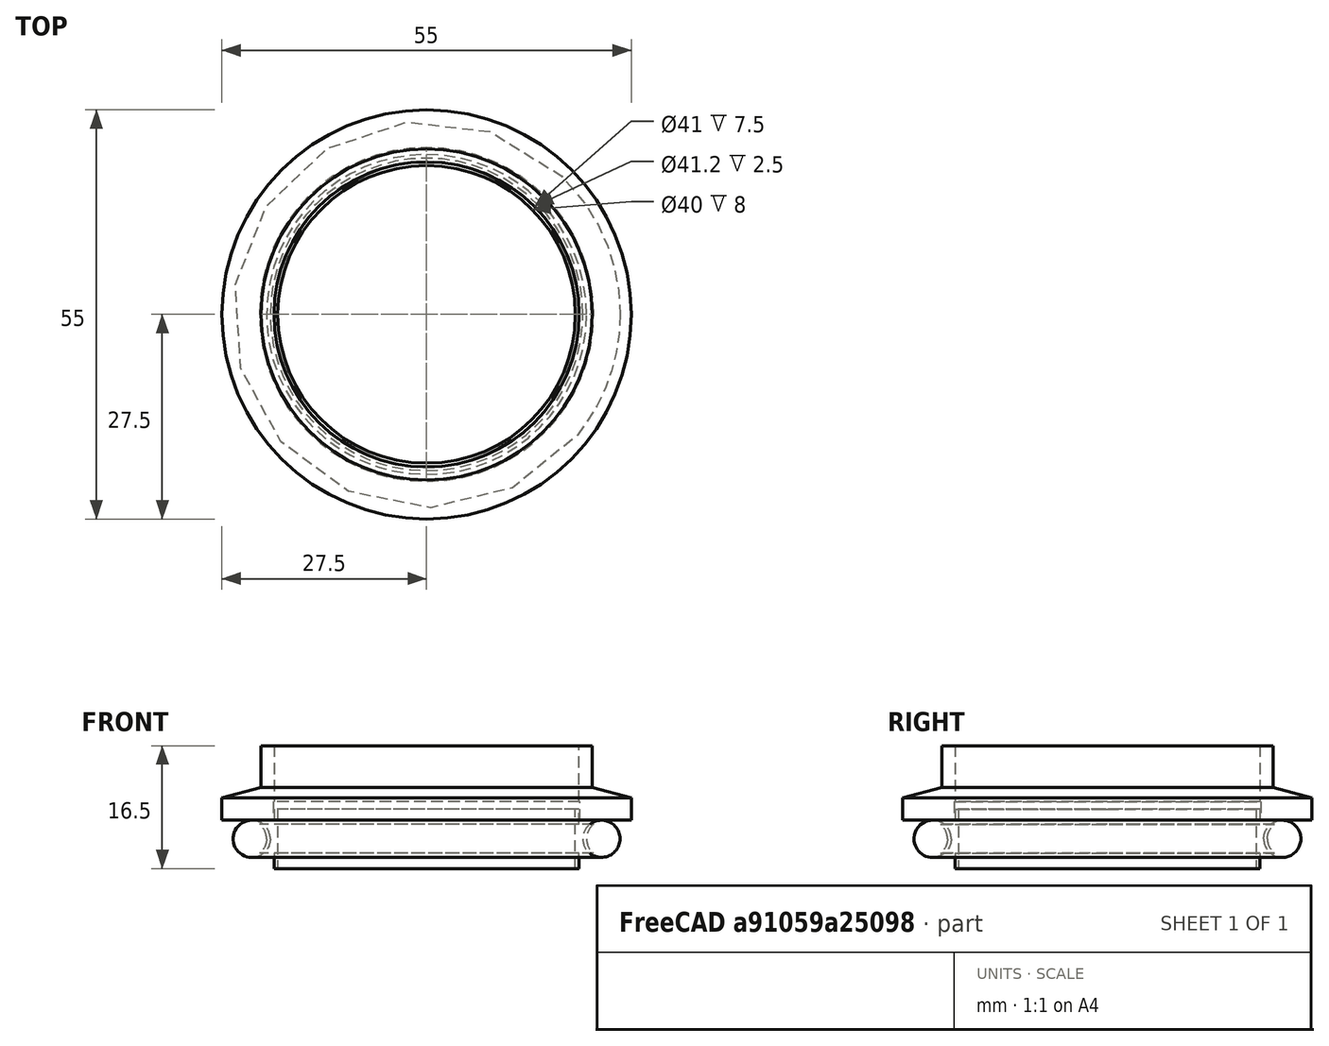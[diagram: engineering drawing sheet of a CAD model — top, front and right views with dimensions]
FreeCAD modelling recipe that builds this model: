
FCSTD DOCUMENT  (FreeCAD 1.0R1.0.0)
Label: KFFlange
License: All rights reserved
LicenseURL: http://en.wikipedia.org/wiki/All_rights_reserved
objects: Part::Cylinder×7, Part::MultiFuse×3, Part::Cut×3, Part::Torus×2, Spreadsheet::Sheet×1, Part::Cone×1
note: 16 computed .brp shape members not serialized (recipe doc carries the construction recipe); baked Part::Feature solids carry a one-line shape summary decoded from their .brp

FEATURE [Spreadsheet::Sheet] Spreadsheet  label="KleinFlange"
  KF = 3
  cells = A1='Nominal bore; B1='D: O-ring ID; C1='d1: Pipe OD; D1='d2: Carrier retainer diameter; E1='d3: Coupling OD; F1='d4: Carrier ID; G1='d5: Connecting Pipe Carrier OD; H1='d6: OD to hold Oring in carrier; I1='R: O ring retainer radius (carrier); A2==hiddenref(.KF.String); B2(D)==.B6; C2(d1)==.C6; D2(d2)==.D6; E2(d3)==.E6; F2(d4)==.F6; G2(d5)==.G6; H2(d6)==.H6; I2(R)=; A3='10; B3=15; C3=14; D3=12.2; E3=30; F3=10; G3=12; H3=15.3; A4='16; B4=18; C4=20; D4=17.2; E4=30; F4=16; G4=17; H4=18.5; A5='25; B5=28; C5=28; D5=26.2; E5=40; F5=25; G5=26; H5=28.5; A6='40; B6=42; C6=44.5; D6=41.2; E6=55; F6=40; G6=41; H6=43; A7='50; B7=55; C7=61; D7=52.2; E7=75; F7=50; G7=52; H7=55.5; A9='O Ring; A10='O ring diameter; B10(oring_dia)=5; A11='Inner diameter; B11==B2; A13='Coupling; L13='Coupling calculated properties; A14='Total length; B14(coupling_len)=10; C14='10 is minimum length; L14='Taper height; M14(coupling_taper_height)==(d3 - d1) / (2 * tan(90 - 15)); A15='Pipe diameter; B15(pipe_dia_user)=100; C15='Maximum specified by d5 (Connecting pipe diameter); L15='Effective pipe diameter; M15(coupling_pipe_ID)==min(d5; pipe_dia_user); L16='Effective coupling length; M16(coupling_len_eff)==min(coupling_len; 10); A17='O Ring carrier interface; A18='O ring carrier recess; B18(oring_recess)=2.5; C18='>= 2.5 by norm
  expr: .KF.Enum = cells[<<A3:|>>]
  expr: .cells.Bind.B2.I2 = tuple(.cells; <<B>> + str(hiddenref(KF) + 3); <<I>> + str(hiddenref(KF) + 3))
FEATURE [Part::Cylinder] Cylinder
  Angle = 360
  AttacherType = Attacher::AttachEngine3D
  FirstAngle = 0
  Height = 3
  Radius = 27.5
  SecondAngle = 0
  expr: Radius = <<KleinFlange>>.d3 / 2
FEATURE [Part::Cone] Cone
  Angle = 360
  AttacherType = Attacher::AttachEngine3D
  Height = 1.40673
  Placement = pos=(0,0,3) rot=(0,0,1;0rad)
  Radius1 = 27.5
  Radius2 = 22.25
  expr: Height = <<KleinFlange>>.coupling_taper_height
  expr: Radius1 = <<KleinFlange>>.d3 / 2
  expr: Radius2 = <<KleinFlange>>.d1 / 2
FEATURE [Part::Cylinder] Cylinder001
  Angle = 360
  AttacherType = Attacher::AttachEngine3D
  FirstAngle = 0
  Height = 10
  Radius = 22.25
  SecondAngle = 0
  expr: Height = <<KleinFlange>>.coupling_len_eff
  expr: Radius = <<KleinFlange>>.d1 / 2
FEATURE [Part::MultiFuse] Fusion
  Shapes = -> [Cylinder001,Cylinder,Cone]
FEATURE [Part::Cylinder] Cylinder002
  Angle = 360
  AttacherType = Attacher::AttachEngine3D
  FirstAngle = 0
  Height = 2.5
  Radius = 20.6
  SecondAngle = 0
  expr: Height = <<KleinFlange>>.oring_recess
  expr: Radius = <<KleinFlange>>.d2 / 2
FEATURE [Part::Cylinder] Cylinder003
  Angle = 360
  AttacherType = Attacher::AttachEngine3D
  FirstAngle = 0
  Height = 10
  Radius = 20.5
  SecondAngle = 0
  expr: Height = <<KleinFlange>>.coupling_len
  expr: Radius = <<KleinFlange>>.coupling_pipe_ID / 2
FEATURE [Part::MultiFuse] Fusion001
  Shapes = -> [Cylinder002,Cylinder003]
FEATURE [Part::Cut] Cut  label="Coupler"
  Base = -> Fusion
  Tool = -> Fusion001
FEATURE [Part::Torus] Torus  label="ORing"
  Angle1 = -180
  Angle2 = 180
  Angle3 = 360
  AttacherType = Attacher::AttachEngine3D
  Placement = pos=(0,0,-2.5) rot=(0,0,1;0rad)
  Radius1 = 23.5
  Radius2 = 2.5
  expr: .Placement.Base.z = -<<KleinFlange>>.oring_dia / 2
  expr: Radius1 = <<KleinFlange>>.D / 2 + <<KleinFlange>>.oring_dia / 2
  expr: Radius2 = <<KleinFlange>>.oring_dia / 2
FEATURE [Part::Cylinder] Cylinder004
  Angle = 360
  AttacherType = Attacher::AttachEngine3D
  FirstAngle = 0
  Height = 8
  Radius = 20.5
  SecondAngle = 0
  expr: Height = <<KleinFlange>>.oring_dia + 3
  expr: Radius = <<KleinFlange>>.d5 / 2
FEATURE [Part::Cylinder] Cylinder005
  Angle = 360
  AttacherType = Attacher::AttachEngine3D
  FirstAngle = 0
  Height = 8
  Radius = 20
  SecondAngle = 0
  expr: Height = <<KleinFlange>>.oring_dia + 3
  expr: Radius = <<KleinFlange>>.d4 / 2
FEATURE [Part::Cylinder] Cylinder006
  Angle = 360
  AttacherType = Attacher::AttachEngine3D
  FirstAngle = 0
  Height = 3.9
  Placement = pos=(0,0,2.05) rot=(0,0,1;0rad)
  Radius = 24
  SecondAngle = 0
  expr: .Placement.Base.z = (<<KleinFlange>>.oring_dia + 3) / 2 - (<<KleinFlange>>.oring_dia - 1.1) / 2
  expr: Height = <<KleinFlange>>.oring_dia - 1.1
  expr: Radius = <<KleinFlange>>.d6 / 2 + <<KleinFlange>>.oring_dia / 2
FEATURE [Part::Torus] Torus001  label="ORing001"
  Angle1 = -180
  Angle2 = 180
  Angle3 = 360
  AttacherType = Attacher::AttachEngine3D
  Placement = pos=(0,0,4) rot=(0,0,1;0rad)
  Radius1 = 24
  Radius2 = 2.5
  expr: .Placement.Base.z = (<<KleinFlange>>.oring_dia + 3) / 2
  expr: Radius1 = <<KleinFlange>>.d6 / 2 + <<KleinFlange>>.oring_dia / 2
  expr: Radius2 = <<KleinFlange>>.oring_dia / 2
FEATURE [Part::MultiFuse] Fusion002
  Shapes = -> [Cylinder006,Cylinder004]
FEATURE [Part::Cut] Cut001
  Base = -> Fusion002
  Tool = -> Torus001
FEATURE [Part::Cut] Cut002  label="ORingCarrier"
  Base = -> Cut001
  Placement = pos=(0,0,-6.5) rot=(0,0,1;0rad)
  Tool = -> Cylinder005
  expr: .Placement.Base.z = -<<KleinFlange>>.oring_dia / 2 - 4
